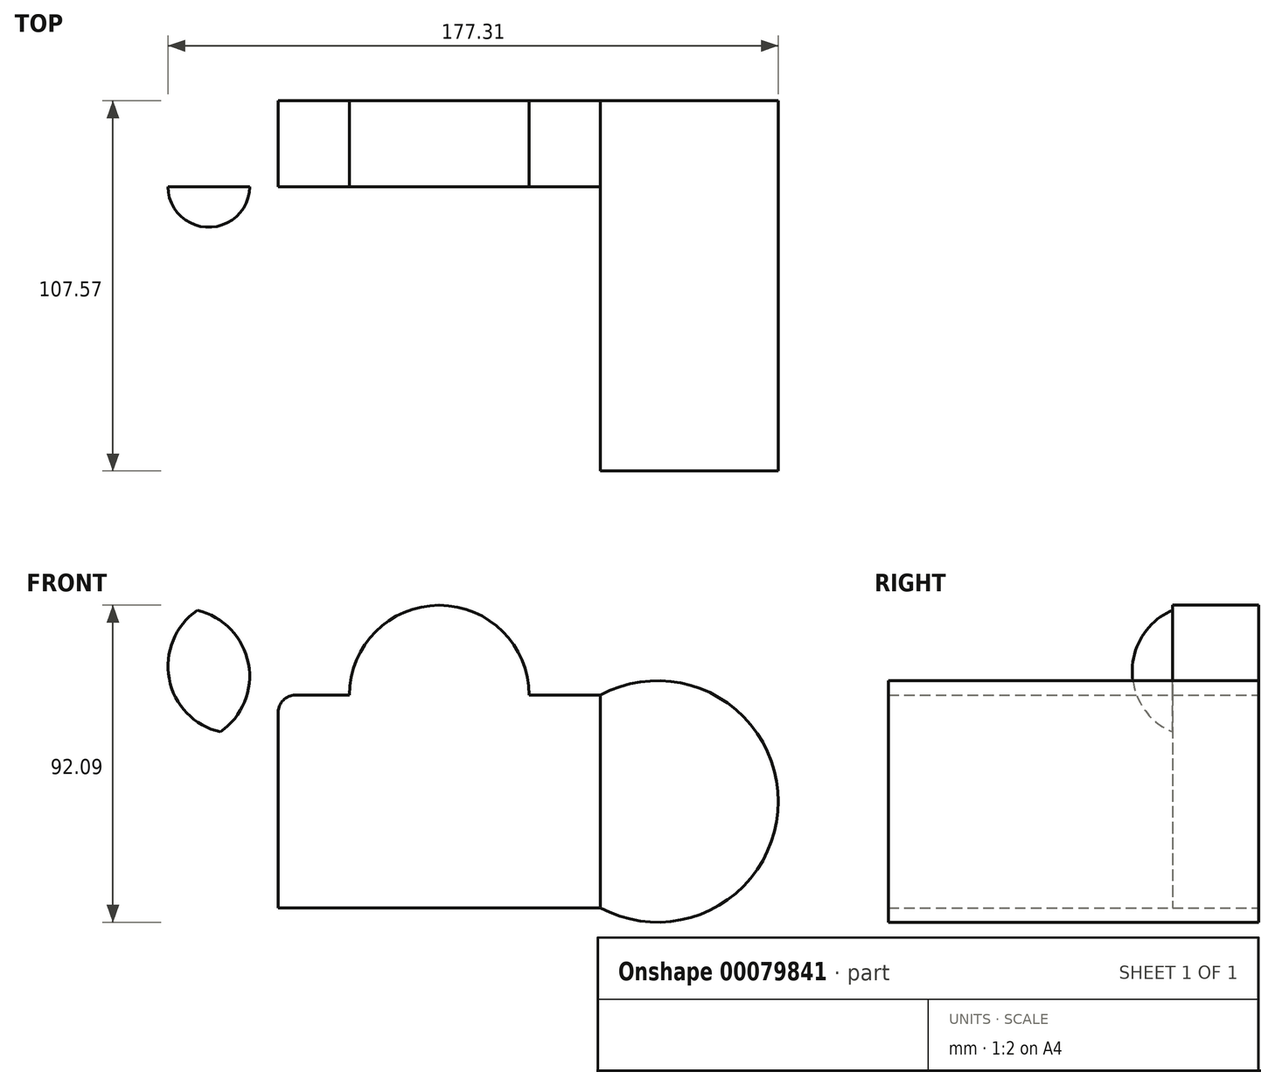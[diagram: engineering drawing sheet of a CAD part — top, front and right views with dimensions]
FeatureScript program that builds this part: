
annotation { "Feature Type Name" : "Feature", "Feature Type Description" : "" }
export const myFeature = defineFeature(function(context is Context, id is Id, definition is map)
    precondition{}
    {
        {
            var Q0;
            Q0=qCreatedBy(makeId("Front.planeOp"),FACE);
            var sketch = newSketch(context, id + "F0", { "sketchPlane" : qUnion([Q0])});
            skLineSegment(sketch, "E0.bottom", {"start": v(-38.16, 31.12) * mm, "end": v(-22.48, 31.12) * mm});
            skLineSegment(sketch, "E0.top", {"start": v(-43.16, -30.67) * mm, "end": v(50.43, -30.67) * mm});
            skLineSegment(sketch, "E0.left", {"start": v(-43.16, 26.12) * mm, "end": v(-43.16, -30.67) * mm});
            skLineSegment(sketch, "E0.right", {"start": v(50.43, 31.12) * mm, "end": v(50.43, -30.67) * mm});
            skArc(sketch, "E1", {"start": v(29.75, 31.12) * mm, "mid": v(3.63, 57.24) * mm, "end": v(-22.48, 31.12) * mm});
            skEllipse(sketch, "E2", {"center": v(-24.53, -63.83) * mm, "majorRadius": 57.7 * mm, "minorRadius": 16.86 * mm, "majorAxis": v(1, 0)});
            skArc(sketch, "E3", {"start": v(50.43, -30.67) * mm, "mid": v(102.13, 0.23) * mm, "end": v(50.43, 31.12) * mm});
            skPoint(sketch, "E4.visualSharp", {"position": v(-43.16, 31.12) * mm});
            skArc(sketch, "E4.filletArc", {"start": v(-38.16, 31.12) * mm, "mid": v(-41.7, 29.66) * mm, "end": v(-43.16, 26.12) * mm});
            skLineSegment(sketch, "E5.trimOffspring", {"start": v(29.75, 31.12) * mm, "end": v(50.43, 31.12) * mm});
            skSolve(sketch);
        }
        {
            var Q0;
            Q0=makeQuery(id+"F0.imprint","IMPRINT",FACE,{"disambiguationData":[TD([[makeQuery(id+"F0.imprint","IMPRINT",EDGE,{"derivedFrom":sQuery(id+"F0.wireOp",EDGE,"E0.bottom")}),-1.0]])]});
            extrude(context, id + "F1", {"entities" : qUnion([Q0]), "depth" : 25 * mm});
        }
        {
            var Q0;
            Q0=makeQuery(id+"F0.imprint","IMPRINT",FACE,{"disambiguationData":[TD([[makeQuery(id+"F0.imprint","IMPRINT",EDGE,{"derivedFrom":sQuery(id+"F0.wireOp",EDGE,"E0.right")}),1.0]])]});
            extrude(context, id + "F2", {"entities" : qUnion([Q0]), "operationType" : NewBodyOperationType.ADD, "depth" : 67.57 * mm});
        }
        {
            var Q0;
            Q0=makeQuery(id+"F2.opExtrude","CAP_FACE",FACE,{"disambiguationData":[OSD([sQuery(id+"F0.wireOp",EDGE,"E0.right"),sQuery(id+"F0.wireOp",EDGE,"E3")])],"isStart":false});
            extrude(context, id + "F3", {"entities" : qUnion([Q0]), "operationType" : NewBodyOperationType.ADD, "depth" : 40 * mm});
        }
        {
            var Q0;
            Q0=makeQuery(id+"F1.opExtrude","CAP_FACE",FACE,{"disambiguationData":[OSD([sQuery(id+"F0.wireOp",EDGE,"E0.bottom"),sQuery(id+"F0.wireOp",EDGE,"E0.top"),sQuery(id+"F0.wireOp",EDGE,"E0.left"),sQuery(id+"F0.wireOp",EDGE,"E0.right"),sQuery(id+"F0.wireOp",EDGE,"E1"),sQuery(id+"F0.wireOp",EDGE,"E4.filletArc"),sQuery(id+"F0.wireOp",EDGE,"E5.trimOffspring")])],"isStart":false});
            var sketch = newSketch(context, id + "F4", { "sketchPlane" : qUnion([Q0])});
            skArc(sketch, "E6", {"start": v(-59.97, 20.44) * mm, "mid": v(-51.8, 40.28) * mm, "end": v(-66.67, 55.74) * mm});
            skLineSegment(sketch, "E7", {"start": v(-66.67, 55.74) * mm, "end": v(-59.97, 20.44) * mm});
            skSolve(sketch);
        }
        {
            var Q0;
            Q0=makeQuery(id+"F4.imprint","IMPRINT",FACE,{"disambiguationData":[TD([[makeQuery(id+"F4.imprint","IMPRINT",EDGE,{"derivedFrom":sQuery(id+"F4.wireOp",EDGE,"E6")}),1.0]])]});
            var Q1;
            Q1=sQuery(id+"F4.wireOp",EDGE,"E7");
            revolve(context, id + "F5", {"entities" : qUnion([Q0]), "axis" : qUnion([Q1]), "revolveType" : RevolveType.ONE_DIRECTION, "angle" : 180 * degree});
        }
    });
